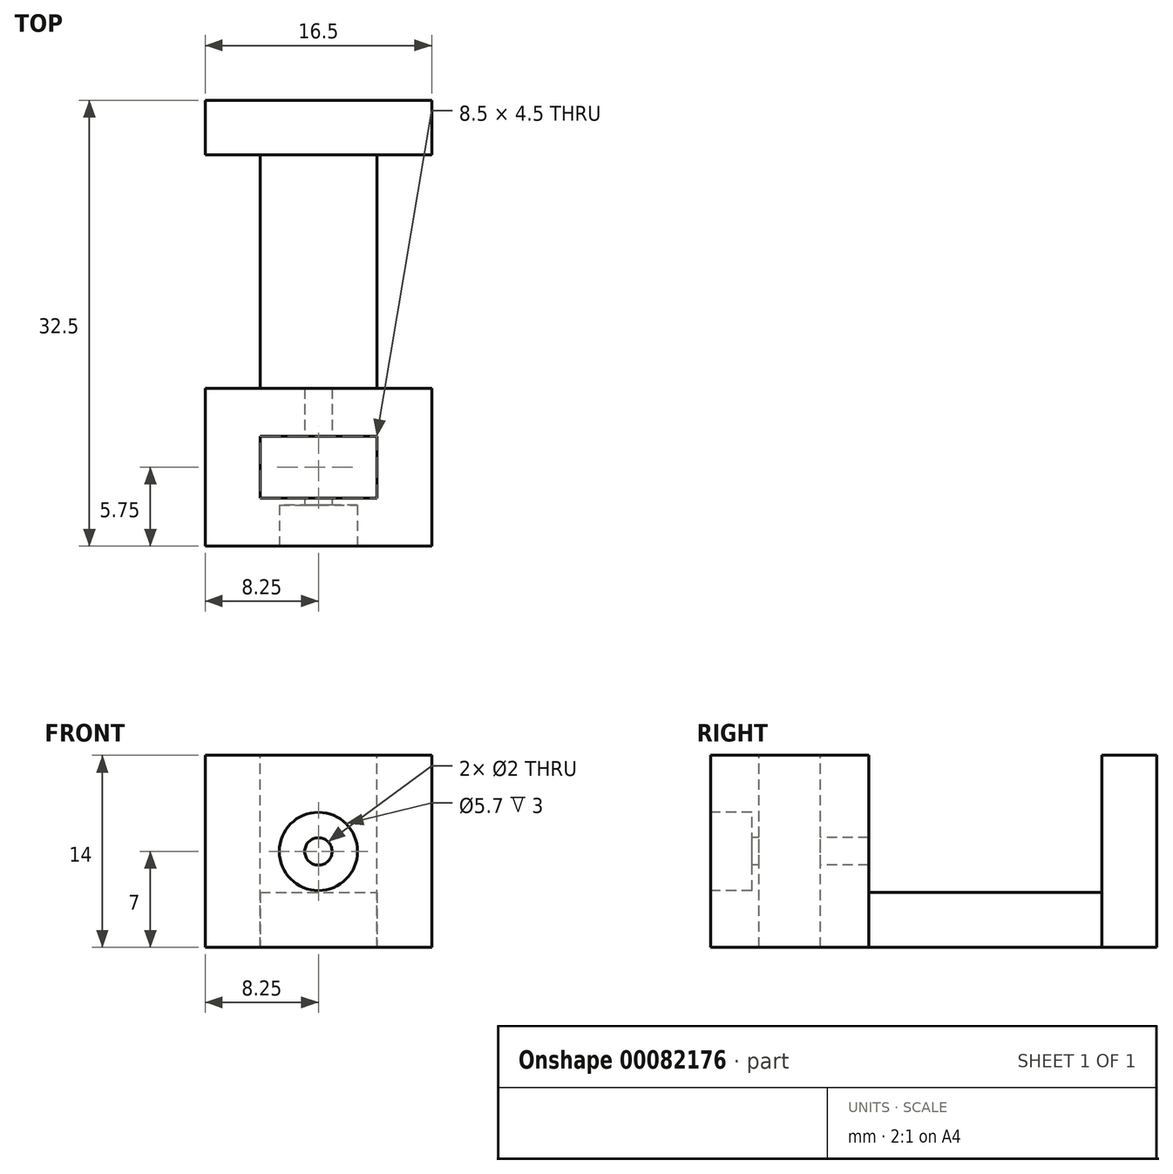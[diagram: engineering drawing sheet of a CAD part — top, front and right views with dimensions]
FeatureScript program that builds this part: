
annotation { "Feature Type Name" : "Feature", "Feature Type Description" : "" }
export const myFeature = defineFeature(function(context is Context, id is Id, definition is map)
    precondition{}
    {
        {
            var Q0;
            Q0=qCreatedBy(makeId("Top.planeOp"),FACE);
            var sketch = newSketch(context, id + "F0", { "sketchPlane" : qUnion([Q0])});
            skLineSegment(sketch, "E0.bottom", {"start": v(-8.25, 16.25) * mm, "end": v(8.25, 16.25) * mm});
            skLineSegment(sketch, "E0.top", {"start": v(-8.25, -16.25) * mm, "end": v(8.25, -16.25) * mm});
            skLineSegment(sketch, "E0.left", {"start": v(-8.25, 16.25) * mm, "end": v(-8.25, -16.25) * mm});
            skLineSegment(sketch, "E0.right", {"start": v(8.25, 16.25) * mm, "end": v(8.25, -16.25) * mm});
            skSolve(sketch);
        }
        {
            var Q0;
            Q0 = qSketchRegion(id + "F0", true);
            extrude(context, id + "F1", {"entities" : qUnion([Q0]), "depth" : 14 * mm});
        }
        {
            var Q0;
            Q0=makeQuery(id+"F1.opExtrude","CAP_FACE",FACE,{"disambiguationData":[OSD([sQuery(id+"F0.wireOp",EDGE,"E0.bottom"),sQuery(id+"F0.wireOp",EDGE,"E0.top"),sQuery(id+"F0.wireOp",EDGE,"E0.left"),sQuery(id+"F0.wireOp",EDGE,"E0.right")])],"isStart":false});
            var sketch = newSketch(context, id + "F2", { "sketchPlane" : qUnion([Q0])});
            skLineSegment(sketch, "E1.bottom", {"start": v(-8.25, -4.25) * mm, "end": v(8.25, -4.25) * mm, "construction": true});
            skLineSegment(sketch, "E1.top", {"start": v(-8.25, -16.25) * mm, "end": v(8.25, -16.25) * mm, "construction": true});
            skLineSegment(sketch, "E1.left", {"start": v(-8.25, -4.25) * mm, "end": v(-8.25, -16.25) * mm, "construction": true});
            skLineSegment(sketch, "E1.right", {"start": v(8.25, -4.25) * mm, "end": v(8.25, -16.25) * mm, "construction": true});
            skSolve(sketch);
        }
        {
            var Q0;
            Q0=makeQuery(id+"F2.imprint","IMPRINT",FACE,{"disambiguationData":[TD([[makeQuery(id+"F2.imprint","IMPRINT",EDGE,{"derivedFrom":makeQuery(id+"F1.opExtrude","CAP_EDGE",EDGE,{"disambiguationData":[OSD([sQuery(id+"F0.wireOp",EDGE,"E0.bottom")])],"isStart":false})}),-1.0]])]});
            var sketch = newSketch(context, id + "F3", { "sketchPlane" : qUnion([Q0])});
            skLineSegment(sketch, "E2.bottom", {"start": v(-8.25, 12.25) * mm, "end": v(8.25, 12.25) * mm});
            skLineSegment(sketch, "E2.top", {"start": v(-8.25, -4.75) * mm, "end": v(8.25, -4.75) * mm});
            skLineSegment(sketch, "E2.left", {"start": v(-8.25, 12.25) * mm, "end": v(-8.25, -4.75) * mm});
            skLineSegment(sketch, "E2.right", {"start": v(8.25, 12.25) * mm, "end": v(8.25, -4.75) * mm});
            skSolve(sketch);
        }
        {
            var Q0;
            Q0 = qSketchRegion(id + "F3", true);
            extrude(context, id + "F4", {"entities" : qUnion([Q0]), "operationType" : NewBodyOperationType.REMOVE, "oppositeDirection" : true, "depth" : 10 * mm});
        }
        {
            var Q0;
            Q0=makeQuery(id+"F1.opExtrude","CAP_FACE",FACE,{"disambiguationData":[OSD([sQuery(id+"F0.wireOp",EDGE,"E0.bottom"),sQuery(id+"F0.wireOp",EDGE,"E0.top"),sQuery(id+"F0.wireOp",EDGE,"E0.left"),sQuery(id+"F0.wireOp",EDGE,"E0.right")])],"isStart":true});
            var sketch = newSketch(context, id + "F5", { "sketchPlane" : qUnion([Q0])});
            skLineSegment(sketch, "E3.bottom", {"start": v(-8.25, -12.25) * mm, "end": v(-4.25, -12.25) * mm});
            skLineSegment(sketch, "E3.top", {"start": v(-8.25, 4.75) * mm, "end": v(-4.25, 4.75) * mm});
            skLineSegment(sketch, "E3.left", {"start": v(-8.25, -12.25) * mm, "end": v(-8.25, 4.75) * mm});
            skLineSegment(sketch, "E3.right", {"start": v(-4.25, -12.25) * mm, "end": v(-4.25, 4.75) * mm});
            skLineSegment(sketch, "E4.bottom", {"start": v(4.25, -12.25) * mm, "end": v(8.25, -12.25) * mm});
            skLineSegment(sketch, "E4.top", {"start": v(4.25, 4.75) * mm, "end": v(8.25, 4.75) * mm});
            skLineSegment(sketch, "E4.left", {"start": v(4.25, -12.25) * mm, "end": v(4.25, 4.75) * mm});
            skLineSegment(sketch, "E4.right", {"start": v(8.25, -12.25) * mm, "end": v(8.25, 4.75) * mm});
            skSolve(sketch);
        }
        {
            var Q0;
            Q0 = qSketchRegion(id + "F5", true);
            extrude(context, id + "F6", {"entities" : qUnion([Q0]), "operationType" : NewBodyOperationType.REMOVE, "endBound" : BoundingType.THROUGH_ALL, "oppositeDirection" : true, "depth" : 25 * mm});
        }
        {
            var Q0;
            Q0=makeQuery(id+"F2.imprint","IMPRINT",FACE,{"disambiguationData":[TD([[makeQuery(id+"F2.imprint","IMPRINT",EDGE,{"derivedFrom":makeQuery(id+"F1.opExtrude","CAP_EDGE",EDGE,{"disambiguationData":[OSD([sQuery(id+"F0.wireOp",EDGE,"E0.bottom")])],"isStart":false})}),-1.0]])]});
            var sketch = newSketch(context, id + "F7", { "sketchPlane" : qUnion([Q0])});
            skLineSegment(sketch, "E5.bottom", {"start": v(-4.25, -8.25) * mm, "end": v(4.25, -8.25) * mm});
            skLineSegment(sketch, "E5.top", {"start": v(-4.25, -12.75) * mm, "end": v(4.25, -12.75) * mm});
            skLineSegment(sketch, "E5.left", {"start": v(-4.25, -8.25) * mm, "end": v(-4.25, -12.75) * mm});
            skLineSegment(sketch, "E5.right", {"start": v(4.25, -8.25) * mm, "end": v(4.25, -12.75) * mm});
            skSolve(sketch);
        }
        {
            var Q0;
            Q0 = qSketchRegion(id + "F7", true);
            extrude(context, id + "F8", {"entities" : qUnion([Q0]), "operationType" : NewBodyOperationType.REMOVE, "endBound" : BoundingType.THROUGH_ALL, "oppositeDirection" : true, "depth" : 25 * mm});
        }
        {
            var Q0;
            Q0=makeQuery(id+"F1.opExtrude","SWEPT_FACE",FACE,{"disambiguationData":[OSD([sQuery(id+"F0.wireOp",EDGE,"E0.top")])]});
            var sketch = newSketch(context, id + "F9", { "sketchPlane" : qUnion([Q0])});
            skLineSegment(sketch, "E6", {"start": v(0, 14) * mm, "end": v(0, 0) * mm, "construction": true});
            skCircle(sketch, "E7", {"center": v(0, 7) * mm, "radius": 2.85 * mm});
            skSolve(sketch);
        }
        {
            var Q0;
            Q0 = qSketchRegion(id + "F9", true);
            extrude(context, id + "F10", {"entities" : qUnion([Q0]), "operationType" : NewBodyOperationType.REMOVE, "oppositeDirection" : true, "depth" : 3 * mm});
        }
        {
            var Q0;
            Q0=makeQuery(id+"F10.boolean.opBoolean","COPY",FACE,{"derivedFrom":makeQuery(id+"F10.opExtrude","CAP_FACE",FACE,{"disambiguationData":[OSD([sQuery(id+"F9.wireOp",EDGE,"E7")])],"isStart":false})});
            var sketch = newSketch(context, id + "F11", { "sketchPlane" : qUnion([Q0])});
            skCircle(sketch, "E8", {"center": v(0, 7) * mm, "radius": 1 * mm});
            skSolve(sketch);
        }
        {
            var Q0;
            Q0 = qSketchRegion(id + "F11", true);
            extrude(context, id + "F12", {"entities" : qUnion([Q0]), "operationType" : NewBodyOperationType.REMOVE, "oppositeDirection" : true, "depth" : 10 * mm});
        }
    });
